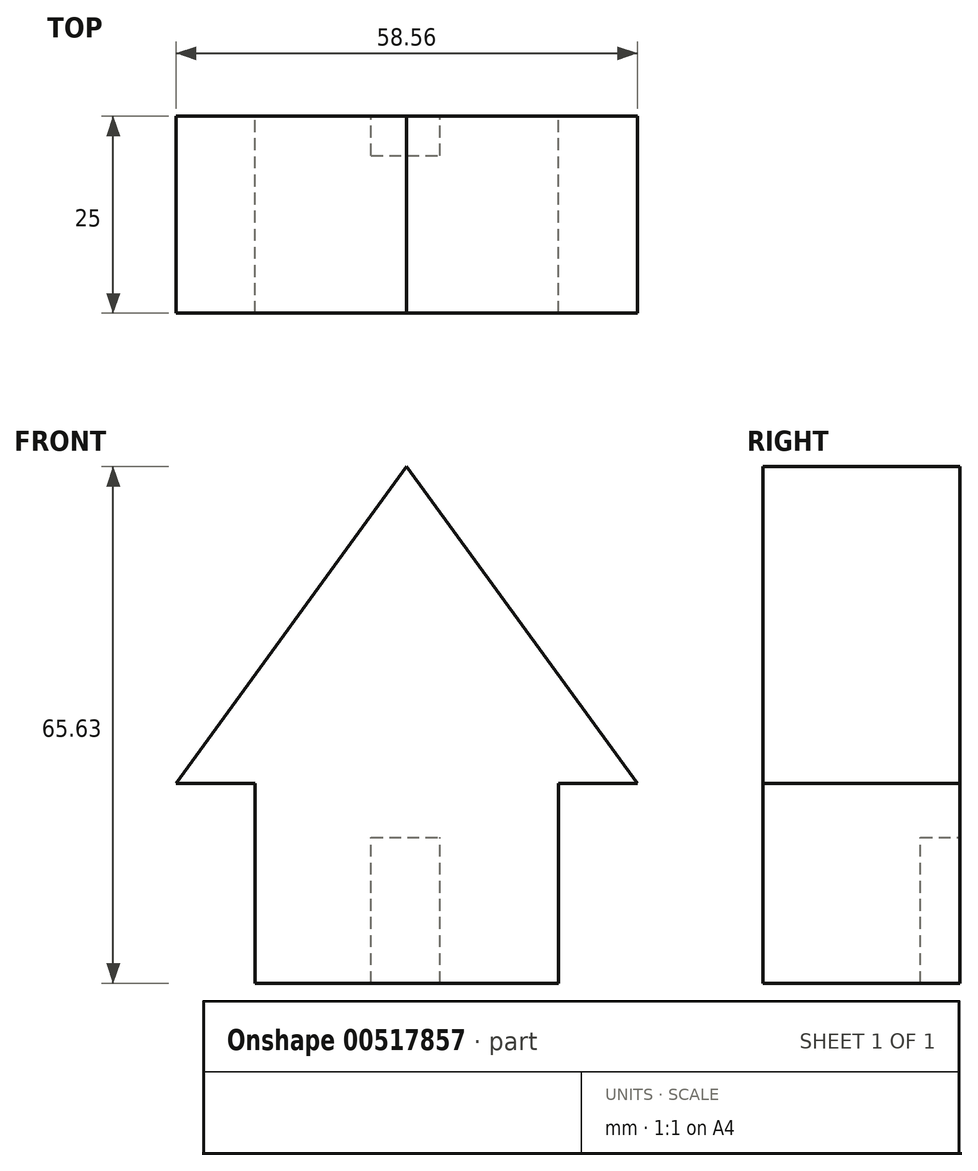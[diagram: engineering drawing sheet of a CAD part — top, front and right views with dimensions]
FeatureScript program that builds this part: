
annotation { "Feature Type Name" : "Feature", "Feature Type Description" : "" }
export const myFeature = defineFeature(function(context is Context, id is Id, definition is map)
    precondition{}
    {
        {
            var Q0;
            Q0=qCreatedBy(makeId("Front.planeOp"),FACE);
            var sketch = newSketch(context, id + "F0", { "sketchPlane" : qUnion([Q0])});
            skLineSegment(sketch, "E0.bottom", {"start": v(19.28, 12.7) * mm, "end": v(-19.28, 12.7) * mm});
            skLineSegment(sketch, "E0.top", {"start": v(19.28, -12.7) * mm, "end": v(-19.28, -12.7) * mm});
            skLineSegment(sketch, "E0.left", {"start": v(19.28, 12.7) * mm, "end": v(19.28, -12.7) * mm});
            skLineSegment(sketch, "E0.right", {"start": v(-19.28, 12.7) * mm, "end": v(-19.28, -12.7) * mm});
            skPoint(sketch, "E0.middle", {"position": v(0, 0) * mm});
            skLineSegment(sketch, "E1", {"start": v(-29.28, 12.7) * mm, "end": v(0, 52.93) * mm});
            skLineSegment(sketch, "E2", {"start": v(0, 52.93) * mm, "end": v(29.28, 12.7) * mm});
            skLineSegment(sketch, "E3", {"start": v(29.28, 12.7) * mm, "end": v(-29.28, 12.7) * mm});
            skSolve(sketch);
        }
        {
            var Q0;
            Q0=qCreatedBy(makeId("Front.planeOp"),FACE);
            var sketch = newSketch(context, id + "F1", { "sketchPlane" : qUnion([Q0])});
            skLineSegment(sketch, "E4.bottom", {"start": v(-4.51, -12.7) * mm, "end": v(4.23, -12.7) * mm});
            skLineSegment(sketch, "E4.top", {"start": v(-4.51, 5.83) * mm, "end": v(4.23, 5.83) * mm});
            skLineSegment(sketch, "E4.left", {"start": v(-4.51, -12.7) * mm, "end": v(-4.51, 5.83) * mm});
            skLineSegment(sketch, "E4.right", {"start": v(4.23, -12.7) * mm, "end": v(4.23, 5.83) * mm});
            skSolve(sketch);
        }
        {
            var Q0;
            Q0 = qSketchRegion(id + "F0", true);
            extrude(context, id + "F2", {"entities" : qUnion([Q0]), "depth" : 25 * mm, "offsetDistance" : 25 * mm});
        }
        {
            var Q0;
            Q0 = qSketchRegion(id + "F1", true);
            extrude(context, id + "F3", {"entities" : qUnion([Q0]), "operationType" : NewBodyOperationType.REMOVE, "oppositeDirection" : true, "depth" : -5 * mm, "offsetDistance" : 25 * mm});
        }
    });
